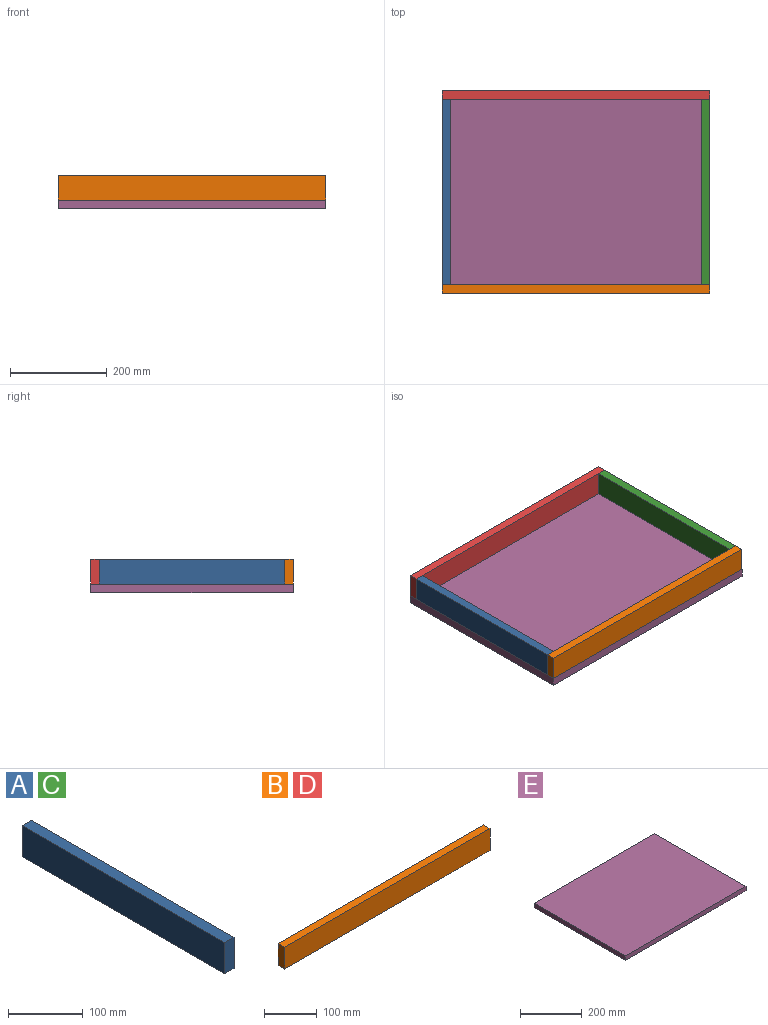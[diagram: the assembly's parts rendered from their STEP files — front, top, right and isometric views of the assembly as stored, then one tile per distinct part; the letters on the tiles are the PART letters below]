
ASSEMBLY  parts=5 mates=4
PART A: 6 faces, bbox 17.6x382.6x50.8 mm
  f0: plane 50.8x17.58mm, normal (0,1,0), area 892.9mm2, adj f1,f3,f4,f5
  f1: plane 382.57x17.58mm, normal (0,0,1), area 6724.4mm2, adj f0,f2,f4,f5
  f2: plane 50.8x17.58mm, normal (0,-1,0), area 892.9mm2, adj f1,f3,f4,f5
  f3: plane 382.57x17.58mm, normal (0,0,-1), area 6724.4mm2, adj f0,f2,f4,f5
  f4: plane 382.57x50.8mm, normal (1,0,0), area 19434.8mm2, adj f0,f1,f2,f3
  f5: plane 382.57x50.8mm, normal (-1,0,0), area 19434.8mm2, adj f0,f1,f2,f3
PART B: 6 faces, bbox 551.1x17.6x50.8 mm
  f0: plane 551.08x17.58mm, normal (0,0,1), area 9686.2mm2, adj f1,f3,f4,f5
  f1: plane 50.8x17.58mm, normal (-1,0,0), area 892.9mm2, adj f0,f2,f4,f5
  f2: plane 551.08x17.58mm, normal (0,0,-1), area 9686.2mm2, adj f1,f3,f4,f5
  f3: plane 50.8x17.58mm, normal (1,0,0), area 892.9mm2, adj f0,f2,f4,f5
  f4: plane 551.08x50.8mm, normal (0,-1,0), area 27994.8mm2, adj f0,f1,f2,f3
  f5: plane 551.08x50.8mm, normal (0,1,0), area 27994.8mm2, adj f0,f1,f2,f3
PART C: same geometry as A
PART D: same geometry as B
PART E: 6 faces, bbox 551.1x417.7x17.6 mm
  f0: plane 551.08x17.58mm, normal (0,1,0), area 9686.2mm2, adj f1,f3,f4,f5
  f1: plane 417.73x17.58mm, normal (-1,0,0), area 7342.3mm2, adj f0,f2,f4,f5
  f2: plane 551.08x17.58mm, normal (0,-1,0), area 9686.2mm2, adj f1,f3,f4,f5
  f3: plane 417.73x17.58mm, normal (1,0,0), area 7342.3mm2, adj f0,f2,f4,f5
  f4: plane 551.08x417.73mm, normal (0,0,1), area 230201.1mm2, adj f0,f1,f2,f3
  f5: plane 551.08x417.73mm, normal (0,0,-1), area 230201.1mm2, adj f0,f1,f2,f3
PLACE A t=(-280.98,-10.39,177.01)mm
PLACE B t=(15.26,-146.47,104.34)mm
PLACE C t=(252.53,-10.39,177.01)mm
PLACE D t=(15.26,253.68,104.34)mm
PLACE E at identity
MATE fastened D.f4 <-> A.f0  axis (0,-1,0) through (-280.98,236.1,42.98)mm
MATE fastened D.f4 <-> C.f0  axis (0,-1,0) through (270.1,236.1,42.98)mm
MATE fastened C.f3 <-> E.f4  axis (0,0,-1) through (270.1,44.82,17.58)mm
MATE fastened C.f2 <-> B.f5  axis (0,-1,0) through (270.1,-146.47,42.98)mm
